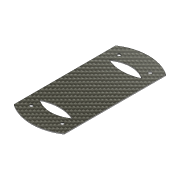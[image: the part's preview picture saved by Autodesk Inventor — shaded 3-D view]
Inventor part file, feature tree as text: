
AUTODESK INVENTOR PART (.ipt)
format: ipt  version: 2017 (Build 210142000, 142)  size: 128,512 bytes
history: native  units: mm
features: other x4, extrude x2, sketch x2, reference x2
ambient origin geometry x8: Origin, YZ Plane, XZ Plane, XY Plane, X Axis, Y Axis, Z Axis, Center Point
bodies: Body1 (feature_tree)
feature tree (10):
  other  "Bryła1"
  extrude  "Wyciągnięcie proste1"  Depth=4.0mm
  extrude  "Wyciągnięcie proste2"  Depth=1.0mm TaperAngle=0.0deg
  sketch  "Szkic1"
  sketch  "Szkic2"
  reference  "Odniesienie9"
  reference  "Odniesienie10"
  other  "<userpath>\Desktop\quadrocopter rysunki\zlozenie.iam"
  other  "zlozenie.iam"
  other  "rama:1"
